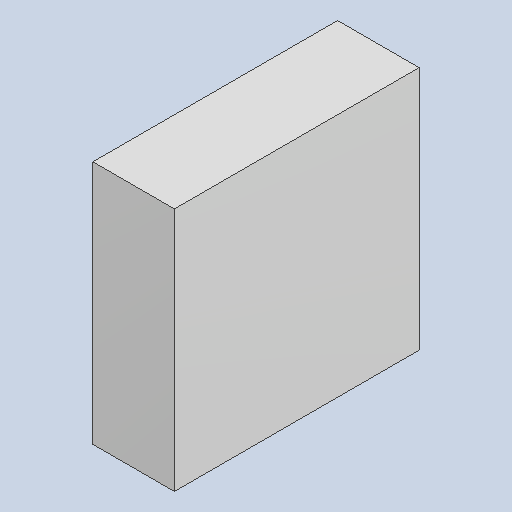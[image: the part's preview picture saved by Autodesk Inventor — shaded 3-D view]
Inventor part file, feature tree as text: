
AUTODESK INVENTOR PART (.ipt)
format: ipt  version: 2023.4 (Build 274418000, 418)  size: 81,408 bytes
history: native  units: mm
features: extrude x1
ambient origin geometry x8: Origin, YZ Plane, XZ Plane, XY Plane, X Axis, Y Axis, Z Axis, Center Point
bodies: Solid1 (feature_tree)
feature tree (1):
  extrude  "Extruded_29"  [1 undecoded]
note: 1 required parameter value undecoded (feature->parameter linkage not recoverable at this tier; creation-order binding heuristic only, values carry confidence <= 0.55)
